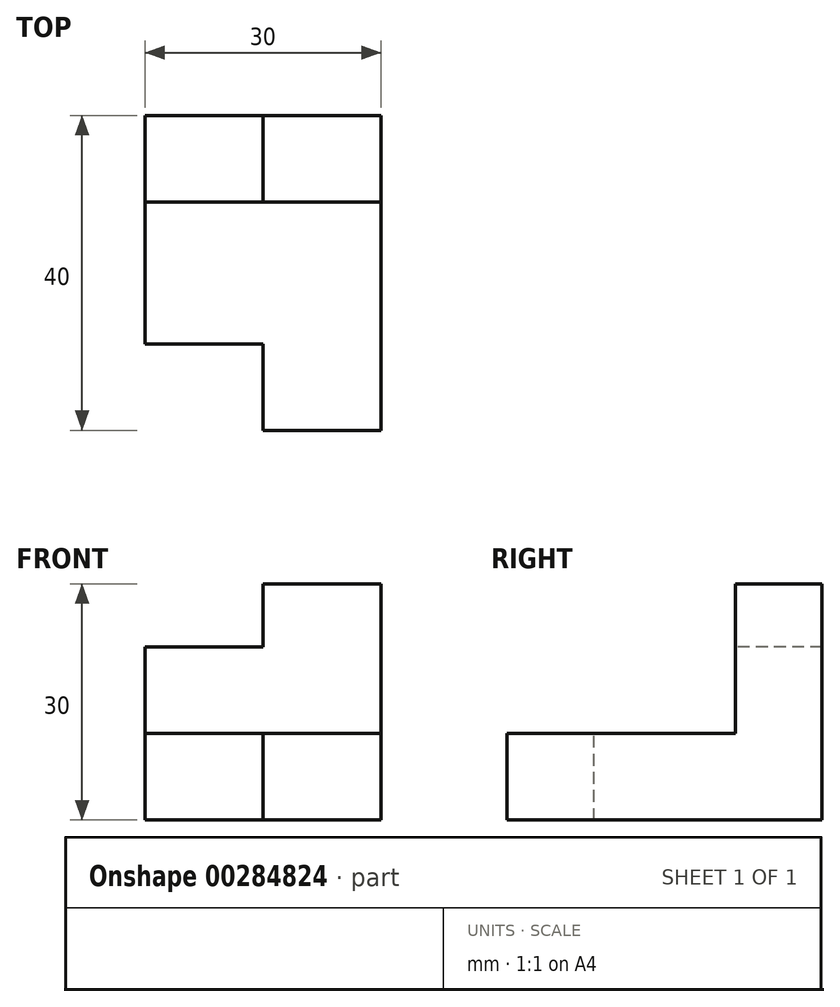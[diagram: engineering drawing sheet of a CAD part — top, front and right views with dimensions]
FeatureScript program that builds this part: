
annotation { "Feature Type Name" : "Feature", "Feature Type Description" : "" }
export const myFeature = defineFeature(function(context is Context, id is Id, definition is map)
    precondition{}
    {
        {
            var Q0;
            Q0=qCreatedBy(makeId("Front.planeOp"),FACE);
            var sketch = newSketch(context, id + "F0", { "sketchPlane" : qUnion([Q0])});
            skLineSegment(sketch, "E0.bottom", {"start": v(0, 0) * mm, "end": v(40, 0) * mm});
            skLineSegment(sketch, "E0.top", {"start": v(0, 30) * mm, "end": v(40, 30) * mm});
            skLineSegment(sketch, "E0.left", {"start": v(0, 0) * mm, "end": v(0, 30) * mm});
            skLineSegment(sketch, "E0.right", {"start": v(40, 0) * mm, "end": v(40, 30) * mm});
            skLineSegment(sketch, "E1.bottom", {"start": v(40, 30) * mm, "end": v(11, 30) * mm});
            skLineSegment(sketch, "E1.top", {"start": v(40, 11) * mm, "end": v(11, 11) * mm});
            skLineSegment(sketch, "E1.left", {"start": v(40, 30) * mm, "end": v(40, 11) * mm});
            skLineSegment(sketch, "E1.right", {"start": v(11, 30) * mm, "end": v(11, 11) * mm});
            skSolve(sketch);
        }
        {
            var Q0;
            Q0=makeQuery(id+"F0.imprint","IMPRINT",FACE,{"disambiguationData":[TD([[makeQuery(id+"F0.imprint","IMPRINT",EDGE,{"derivedFrom":sQuery(id+"F0.wireOp",EDGE,"E0.bottom")}),1.0]])]});
            extrude(context, id + "F1", {"entities" : qUnion([Q0]), "depth" : 30 * mm});
        }
        {
            var Q0;
            Q0=makeQuery(id+"F1.opExtrude","SWEPT_FACE",FACE,{"disambiguationData":[OSD([sQuery(id+"F0.wireOp",EDGE,"E1.top")])]});
            var sketch = newSketch(context, id + "F2", { "sketchPlane" : qUnion([Q0])});
            skPoint(sketch, "E2.oppositeSnap0", {"position": v(40, -15) * mm});
            skLineSegment(sketch, "E2.bottom", {"start": v(40, -30) * mm, "end": v(29, -30) * mm});
            skLineSegment(sketch, "E2.top", {"start": v(40, -15) * mm, "end": v(29, -15) * mm});
            skLineSegment(sketch, "E2.left", {"start": v(40, -30) * mm, "end": v(40, -15) * mm});
            skLineSegment(sketch, "E2.right", {"start": v(29, -30) * mm, "end": v(29, -15) * mm});
            skSolve(sketch);
        }
        {
            var Q0;
            Q0 = qSketchRegion(id + "F2", true);
            var Q1;
            Q1=makeQuery(id+"F1.opExtrude","CAP_VERTEX",VERTEX,{"disambiguationData":[OSD([sQuery(id+"F0.wireOp",EDGE,"E0.bottom"),sQuery(id+"F0.wireOp",EDGE,"E0.right")])],"isStart":false});
            extrude(context, id + "F3", {"entities" : qUnion([Q0]), "operationType" : NewBodyOperationType.REMOVE, "endBound" : BoundingType.UP_TO_VERTEX, "oppositeDirection" : true, "endBoundEntityVertex" : qUnion([Q1]), "depth" : 25 * mm});
        }
        {
            var Q0;
            Q0=makeQuery(id+"F1.opExtrude","SWEPT_FACE",FACE,{"disambiguationData":[OSD([sQuery(id+"F0.wireOp",EDGE,"E1.right")])]});
            var sketch = newSketch(context, id + "F4", { "sketchPlane" : qUnion([Q0])});
            skPoint(sketch, "E3.oppositeSnap0", {"position": v(-15, 30) * mm});
            skLineSegment(sketch, "E3.bottom", {"start": v(-30, 30) * mm, "end": v(-15, 30) * mm});
            skLineSegment(sketch, "E3.top", {"start": v(-30, 22) * mm, "end": v(-15, 22) * mm});
            skLineSegment(sketch, "E3.left", {"start": v(-30, 30) * mm, "end": v(-30, 22) * mm});
            skLineSegment(sketch, "E3.right", {"start": v(-15, 30) * mm, "end": v(-15, 22) * mm});
            skSolve(sketch);
        }
        {
            var Q0;
            Q0 = qSketchRegion(id + "F4", true);
            var Q1;
            Q1=makeQuery(id+"F1.opExtrude","CAP_VERTEX",VERTEX,{"disambiguationData":[OSD([sQuery(id+"F0.wireOp",EDGE,"E0.top"),sQuery(id+"F0.wireOp",EDGE,"E0.left")])],"isStart":false});
            extrude(context, id + "F5", {"entities" : qUnion([Q0]), "operationType" : NewBodyOperationType.REMOVE, "endBound" : BoundingType.UP_TO_VERTEX, "oppositeDirection" : true, "endBoundEntityVertex" : qUnion([Q1]), "depth" : 25 * mm});
        }
        {
            var Q0;
            Q0=makeQuery(id+"F1.opExtrude","SWEPT_BODY",BODY,{"disambiguationData":[OSD([sQuery(id+"F0.wireOp",EDGE,"E0.bottom"),sQuery(id+"F0.wireOp",EDGE,"E0.top"),sQuery(id+"F0.wireOp",EDGE,"E0.left"),sQuery(id+"F0.wireOp",EDGE,"E0.right"),sQuery(id+"F0.wireOp",EDGE,"E1.top"),sQuery(id+"F0.wireOp",EDGE,"E1.right")])]});
            var Q1;
            Q1=makeQuery(id+"F1.opExtrude","CAP_EDGE",EDGE,{"disambiguationData":[OSD([sQuery(id+"F0.wireOp",EDGE,"E0.left")])],"isStart":true});
            transform(context, id + "F6", {"entities" : qUnion([Q0]), "transformType" : TransformType.ROTATION, "transformAxis" : qUnion([Q1]), "angle" : 90 * degree, "oppositeDirection" : true, "makeCopy" : false});
        }
    });
